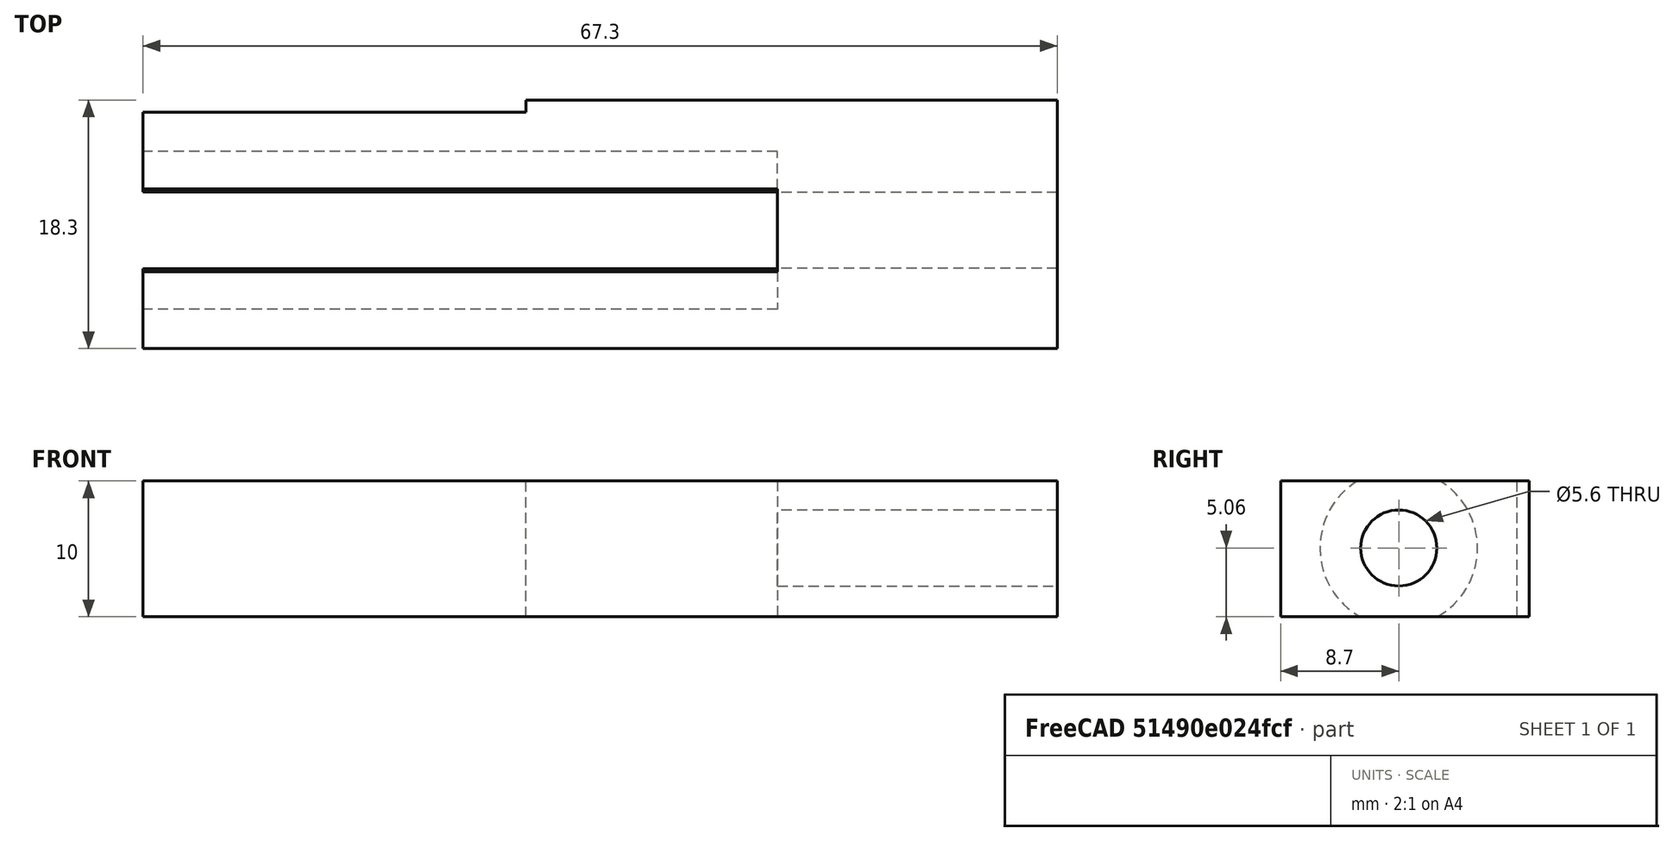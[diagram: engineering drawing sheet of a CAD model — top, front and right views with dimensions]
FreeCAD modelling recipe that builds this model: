
FCSTD DOCUMENT  (FreeCAD 1.0R1.0.0)
Label: AIWA_LIB_902_to_10440
License: All rights reserved
LicenseURL: http://en.wikipedia.org/wiki/All_rights_reserved
objects: Part::Cut×3, Part::Box×2, Part::Cylinder×2, Spreadsheet::Sheet×1, Part::Feature×1
note: 8 computed .brp shape members not serialized (recipe doc carries the construction recipe); baked Part::Feature solids carry a one-line shape summary decoded from their .brp

FEATURE [Spreadsheet::Sheet] Spreadsheet  label="AdapterParameters"
  cells = A2='Length; B2(length)=67.3; C2=67.4; A3='Thickness; B3(thickness)=10; C3=10.1; A4='Width 1; B4(w1)=17.4; C4=17.6; A5='Width 2; B5(w2)=18.3; C5=18.5; A6='Step length; B6(steplen)=39.1; C6=28.3; D6='Unknown; E6=39.1; F6=28.3; A7='Spring diameter; B7(spring_dia)=5.6; C7=5.5
FEATURE [Part::Box] Box  label="Cube"
  AttacherType = Attacher::AttachEngine3D
  Height = 10
  Length = 67.3
  Width = 18.3
  expr: Height = <<AdapterParameters>>.thickness
  expr: Length = <<AdapterParameters>>.length
  expr: Width = <<AdapterParameters>>.w2
FEATURE [Part::Box] Box001  label="Cube001"
  AttacherType = Attacher::AttachEngine3D
  Height = 10
  Length = 28.2
  Placement = pos=(0,17.4,0) rot=(0,0,1;0rad)
  Width = 0.9
  expr: .Placement.Base.y = <<AdapterParameters>>.w1
  expr: Height = <<AdapterParameters>>.thickness
  expr: Length = <<AdapterParameters>>.length - <<AdapterParameters>>.steplen
  expr: Width = <<AdapterParameters>>.w2 - <<AdapterParameters>>.w1
FEATURE [Part::Cut] Cut
  Base = -> Box
  Tool = -> Box001
FEATURE [Part::Cylinder] Cylinder
  Angle = 360
  AttacherType = Attacher::AttachEngine3D
  FirstAngle = 0
  Height = 46.7
  Placement = pos=(0,8.7,5.06) rot=(0,1,0;1.5708rad)
  Radius = 5.8
  SecondAngle = 0
  expr: .Placement.Base.y = <<AdapterParameters>>.w1 / 2
FEATURE [Part::Feature] OpenSCAD_Model001
  shape: bbox 67.4 x 10.1 x 18.5 mm, 342 faces, 0 solids (baked)
FEATURE [Part::Cut] Cut001
  Base = -> Cut
  Tool = -> Cylinder
FEATURE [Part::Cylinder] Cylinder001
  Angle = 360
  AttacherType = Attacher::AttachEngine3D
  FirstAngle = 0
  Height = 67.3
  Placement = pos=(0,8.7,5.06) rot=(0,1,0;1.5708rad)
  Radius = 2.8
  SecondAngle = 0
  expr: .Placement.Base.y = <<AdapterParameters>>.w1 / 2
  expr: Height = <<AdapterParameters>>.length
  expr: Radius = <<AdapterParameters>>.spring_dia / 2
FEATURE [Part::Cut] Cut002
  Base = -> Cut001
  Tool = -> Cylinder001
